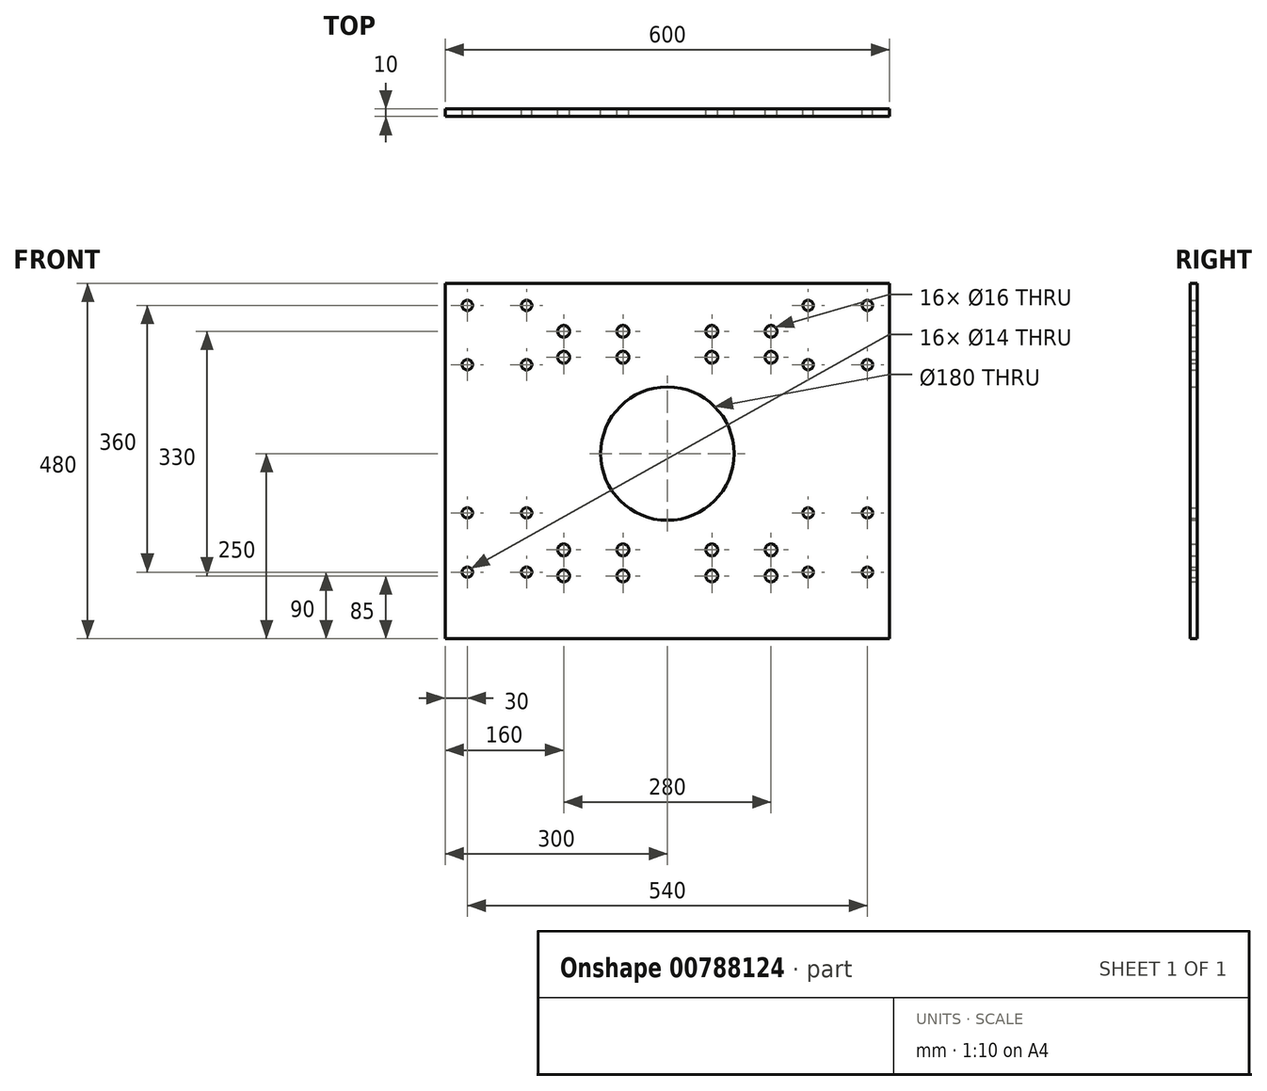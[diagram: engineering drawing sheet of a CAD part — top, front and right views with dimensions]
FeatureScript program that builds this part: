
annotation { "Feature Type Name" : "Feature", "Feature Type Description" : "" }
export const myFeature = defineFeature(function(context is Context, id is Id, definition is map)
    precondition{}
    {
        {
            var Q0;
            Q0=qCreatedBy(makeId("Front.planeOp"),FACE);
            var sketch = newSketch(context, id + "F0", { "sketchPlane" : qUnion([Q0])});
            skLineSegment(sketch, "E0.bottom", {"start": v(-300, -250) * mm, "end": v(300, -250) * mm});
            skLineSegment(sketch, "E0.top", {"start": v(-300, 230) * mm, "end": v(300, 230) * mm});
            skLineSegment(sketch, "E0.left", {"start": v(-300, -250) * mm, "end": v(-300, 230) * mm});
            skLineSegment(sketch, "E0.right", {"start": v(300, -250) * mm, "end": v(300, 230) * mm});
            skPoint(sketch, "E1", {"position": v(0, 230) * mm});
            skPoint(sketch, "E2", {"position": v(-250, 0) * mm});
            skCircle(sketch, "E3", {"center": v(0, 0) * mm, "radius": 90 * mm});
            skCircle(sketch, "E4", {"center": v(-270, 200) * mm, "radius": 7 * mm});
            skCircle(sketch, "E5", {"center": v(-190, 200) * mm, "radius": 7 * mm});
            skCircle(sketch, "E6", {"center": v(190, 200) * mm, "radius": 7 * mm});
            skCircle(sketch, "E7", {"center": v(270, 200) * mm, "radius": 7 * mm});
            skCircle(sketch, "E8", {"center": v(270, -160) * mm, "radius": 7 * mm});
            skCircle(sketch, "E9", {"center": v(-270, -160) * mm, "radius": 7 * mm});
            skCircle(sketch, "E10", {"center": v(-190, -160) * mm, "radius": 7 * mm});
            skCircle(sketch, "E11", {"center": v(190, -160) * mm, "radius": 7 * mm});
            skCircle(sketch, "E12", {"center": v(190, 120) * mm, "radius": 7 * mm});
            skCircle(sketch, "E13", {"center": v(270, 120) * mm, "radius": 7 * mm});
            skCircle(sketch, "E14", {"center": v(190, -80) * mm, "radius": 7 * mm});
            skCircle(sketch, "E15", {"center": v(270, -80) * mm, "radius": 7 * mm});
            skCircle(sketch, "E16", {"center": v(-190, -80) * mm, "radius": 7 * mm});
            skCircle(sketch, "E17", {"center": v(-270, -80) * mm, "radius": 7 * mm});
            skCircle(sketch, "E18", {"center": v(-270, 120) * mm, "radius": 7 * mm});
            skCircle(sketch, "E19", {"center": v(-190, 120) * mm, "radius": 7 * mm});
            skLineSegment(sketch, "E20", {"start": v(-100, 168.3) * mm, "end": v(-100, -291.76) * mm, "construction": true});
            skLineSegment(sketch, "E21", {"start": v(100, 173.27) * mm, "end": v(100, -324.62) * mm, "construction": true});
            skCircle(sketch, "E22", {"center": v(-140, -130) * mm, "radius": 8 * mm});
            skCircle(sketch, "E23", {"center": v(-60, -130) * mm, "radius": 8 * mm});
            skCircle(sketch, "E24", {"center": v(-140, -165) * mm, "radius": 8 * mm});
            skCircle(sketch, "E25", {"center": v(-60, -165) * mm, "radius": 8 * mm});
            skLineSegment(sketch, "E26", {"start": v(0, 230) * mm, "end": v(0, -250) * mm, "construction": true});
            skCircle(sketch, "E27.MirrorC", {"center": v(60, -130) * mm, "radius": 8 * mm});
            skCircle(sketch, "E28.MirrorC", {"center": v(60, -165) * mm, "radius": 8 * mm});
            skCircle(sketch, "E29.MirrorC", {"center": v(140, -165) * mm, "radius": 8 * mm});
            skCircle(sketch, "E30.MirrorC", {"center": v(140, -130) * mm, "radius": 8 * mm});
            skCircle(sketch, "E31", {"center": v(-140, 130) * mm, "radius": 8 * mm});
            skCircle(sketch, "E32", {"center": v(-140, 165) * mm, "radius": 8 * mm});
            skCircle(sketch, "E33", {"center": v(-60, 130) * mm, "radius": 8 * mm});
            skCircle(sketch, "E34", {"center": v(-60, 165) * mm, "radius": 8 * mm});
            skCircle(sketch, "E35", {"center": v(60, 130) * mm, "radius": 8 * mm});
            skCircle(sketch, "E36", {"center": v(140, 130) * mm, "radius": 8 * mm});
            skCircle(sketch, "E37", {"center": v(140, 165) * mm, "radius": 8 * mm});
            skCircle(sketch, "E38", {"center": v(60, 165) * mm, "radius": 8 * mm});
            skSolve(sketch);
        }
        {
            var Q0;
            Q0 = qSketchRegion(id + "F0", true);
            extrude(context, id + "F1", {"entities" : qUnion([Q0]), "depth" : 10 * mm, "offsetDistance" : 25 * mm});
        }
    });
